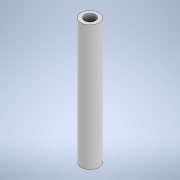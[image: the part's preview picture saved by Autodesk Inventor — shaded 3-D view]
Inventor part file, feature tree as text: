
AUTODESK INVENTOR PART (.ipt)
format: ipt  version: 2020 (Build 240168000, 168)  size: 93,696 bytes
history: native  units: in
note: dims shown in document units (in); Inventor stores cm internally (conversion verified against a paired STEP export)
features: extrude x1, sketch x1
ambient origin geometry x8: Origin, YZ Plane, XZ Plane, XY Plane, X Axis, Y Axis, Z Axis, Center Point
bodies: Solid1 (feature_tree)
feature tree (2):
  extrude  "Extrusion1"  Depth=1.378in
  sketch  "Sketch1"  dims[d0=0.1181in d1=0.1969in d2=1.378in d3=0.0in]
